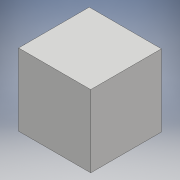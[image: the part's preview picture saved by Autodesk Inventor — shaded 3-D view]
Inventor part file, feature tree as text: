
AUTODESK INVENTOR PART (.ipt)
format: ipt  version: 2017 (Build 210142000, 142)  size: 97,792 bytes
history: native  units: mm
features: extrude x2, sketch x2
ambient origin geometry x8: Origin, YZ Plane, XZ Plane, XY Plane, X Axis, Y Axis, Z Axis, Center Point
bodies: Solid1 (feature_tree)
feature tree (4):
  extrude  "Extrusion1"  Depth=50.0mm
  extrude  "Extrusion2"  Depth=2.0mm
  sketch  "Sketch2"  dims[d0=50.0mm d1=50.0mm]
  sketch  "Sketch3"  dims[d2=4.0mm d3=0.0mm d4=2.0mm d5=45.0mm d6=0.0mm]
